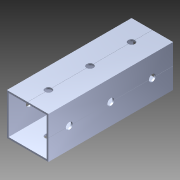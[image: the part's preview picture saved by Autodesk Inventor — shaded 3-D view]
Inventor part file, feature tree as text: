
AUTODESK INVENTOR PART (.ipt)
format: ipt  version: 2014 SP1 (Build 180222100, 222)  size: 1,243,648 bytes
history: native  units: in
note: dims shown in document units (in); Inventor stores cm internally (conversion verified against a paired STEP export)
features: extrude x4, sketch x4, pattern_circular x1, other x1, imported_body x1
ambient origin geometry x8: Origin, YZ Plane, XZ Plane, XY Plane, X Axis, Y Axis, Z Axis, Center Point
bodies: Body1 (feature_tree)
feature tree (11):
  pattern_circular  "CirPattern2"
  other  "1x1 tube1"
  extrude  "Extrusion1"  Depth=4.0in TaperAngle=0.0deg
  extrude  "Extrusion2"  Depth=1.0in TaperAngle=0.0deg
  extrude  "Extrusion3"  [1 undecoded]
  extrude  "Extrusion4"  [1 undecoded]
  imported_body  "Base1"
  sketch  "Sketch1"  dims[d0=50.0in d1=0.0in d2=4.0in d3=0.0in]
  sketch  "Sketch3"  dims[d4=1.0in d5=0.0in d6=1.0in d7=0.0in]
  sketch  "Sketch4"
  sketch  "Sketch5"
note: 2 required parameter values undecoded (feature->parameter linkage not recoverable at this tier; creation-order binding heuristic only, values carry confidence <= 0.55)
